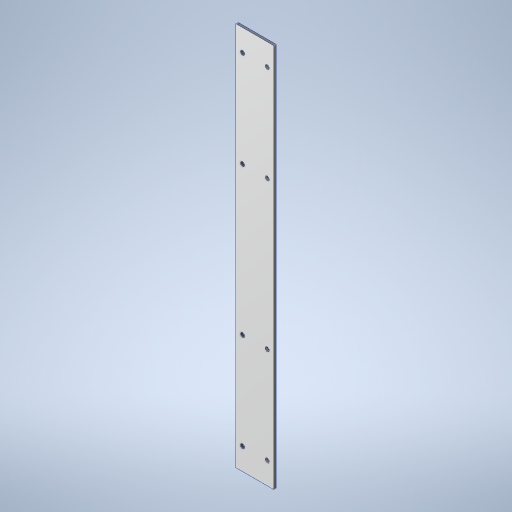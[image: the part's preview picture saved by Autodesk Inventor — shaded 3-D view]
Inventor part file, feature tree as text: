
AUTODESK INVENTOR PART (.ipt)
format: ipt  version: 2024 (Build 280153000, 153)  size: 284,672 bytes
history: native  units: mm
features: extrude x3, other x2, sketch x2, hole x1
ambient origin geometry x8: Origin, YZ Plane, XZ Plane, XY Plane, X Axis, Y Axis, Z Axis, Center Point
bodies: Body1 (feature_tree), Body2 (feature_tree)
feature tree (8):
  other  "Laminate"
  sketch  "Sketch1"  dims[d0=49.5mm d1=499.0mm]
  extrude  "Extrusion1"  Depth=499.0mm
  extrude  "Extrusion2"  Depth=2.9mm TaperAngle=0.0deg
  extrude  "Extrusion3"  Depth=2.9mm TaperAngle=0.0deg
  hole  "Hole1"  [1 undecoded]
  other  "Core"
  sketch  "Sketch2"  dims[d2=3.0mm d3=0.0mm d4=2.9mm d5=0.0mm d6=2.9mm d7=0.0mm d8=32.0mm d10=442.0mm d11=125.0mm d12=5.4mm d13=6.0mm d14=4.0mm d15=2.0mm d16=90.0deg d17=8.0mm d18=20.594885mm]
note: 1 required parameter value undecoded (feature->parameter linkage not recoverable at this tier; creation-order binding heuristic only, values carry confidence <= 0.55)
